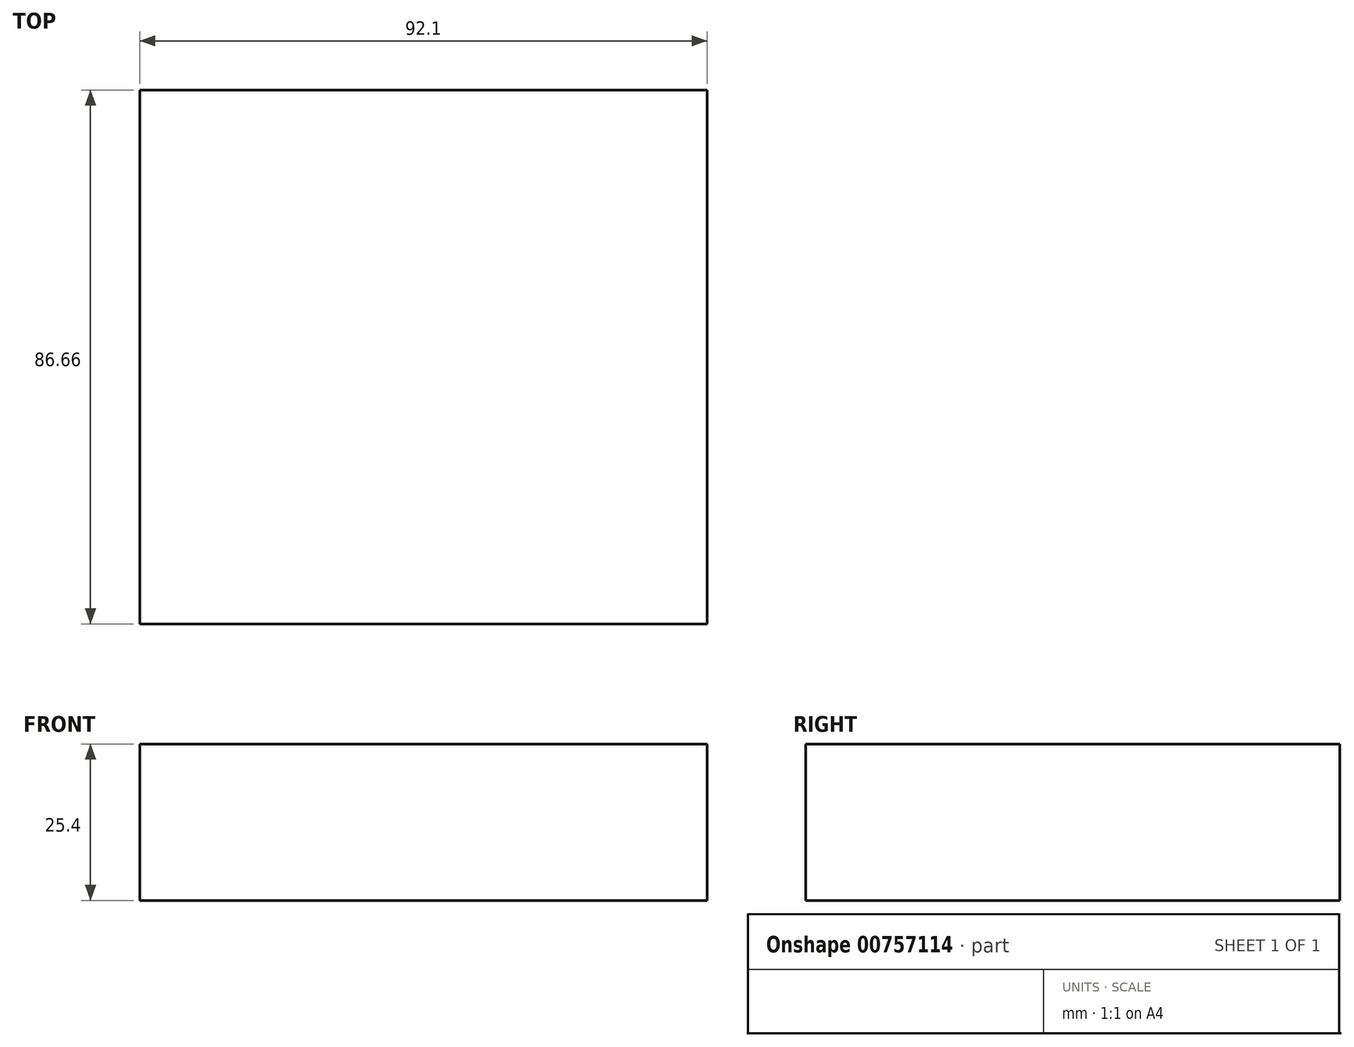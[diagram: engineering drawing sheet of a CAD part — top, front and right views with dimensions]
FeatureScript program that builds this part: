
annotation { "Feature Type Name" : "Feature", "Feature Type Description" : "" }
export const myFeature = defineFeature(function(context is Context, id is Id, definition is map)
    precondition{}
    {
        {
            var Q0;
            Q0=qCreatedBy(makeId("Top.planeOp"),FACE);
            var sketch = newSketch(context, id + "F0", { "sketchPlane" : qUnion([Q0])});
            skLineSegment(sketch, "E0.bottom", {"start": v(-46.05, 43.33) * mm, "end": v(46.05, 43.33) * mm});
            skLineSegment(sketch, "E0.top", {"start": v(-46.05, -43.33) * mm, "end": v(46.05, -43.33) * mm});
            skLineSegment(sketch, "E0.left", {"start": v(-46.05, 43.33) * mm, "end": v(-46.05, -43.33) * mm});
            skLineSegment(sketch, "E0.right", {"start": v(46.05, 43.33) * mm, "end": v(46.05, -43.33) * mm});
            skPoint(sketch, "E0.middle", {"position": v(0, 0) * mm});
            skSolve(sketch);
        }
        {
            var Q0;
            Q0 = qSketchRegion(id + "F0", true);
            extrude(context, id + "F1", {"entities" : qUnion([Q0]), "depth" : 25.4 * mm, "offsetDistance" : 25.4 * mm});
        }
    });
